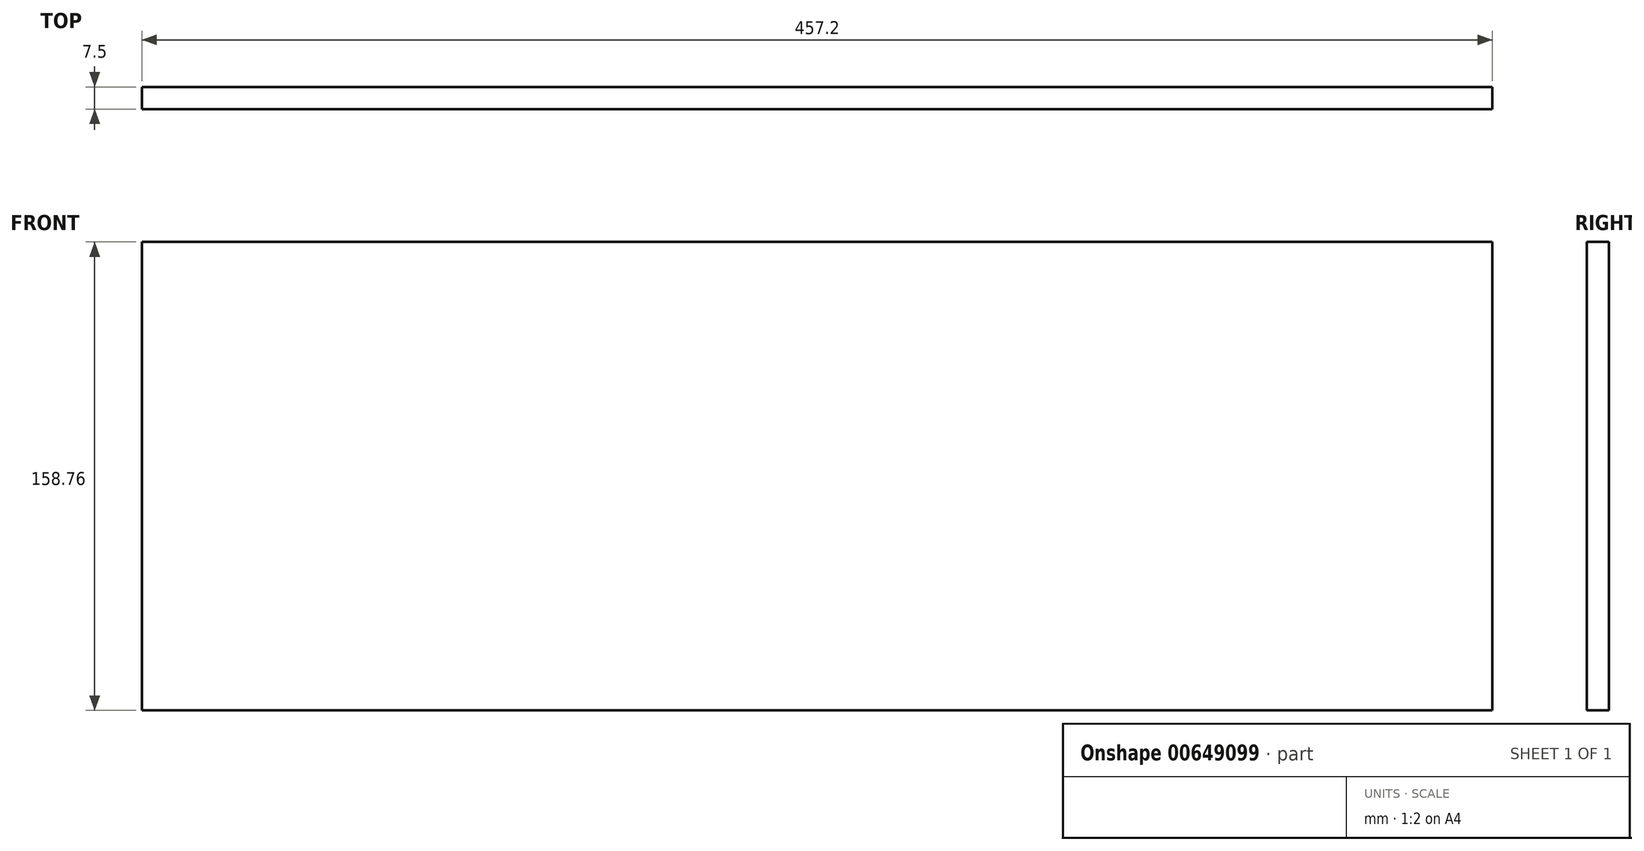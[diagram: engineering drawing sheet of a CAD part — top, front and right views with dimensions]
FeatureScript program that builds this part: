
annotation { "Feature Type Name" : "Feature", "Feature Type Description" : "" }
export const myFeature = defineFeature(function(context is Context, id is Id, definition is map)
    precondition{}
    {
        {
            var Q0;
            Q0=qCreatedBy(makeId("Front.planeOp"),FACE);
            var sketch = newSketch(context, id + "F0", { "sketchPlane" : qUnion([Q0])});
            skLineSegment(sketch, "E0.bottom", {"start": v(-228.6, 79.37) * mm, "end": v(228.6, 79.37) * mm});
            skLineSegment(sketch, "E0.top", {"start": v(-228.6, -79.37) * mm, "end": v(228.6, -79.37) * mm});
            skLineSegment(sketch, "E0.left", {"start": v(-228.6, 79.37) * mm, "end": v(-228.6, -79.37) * mm});
            skLineSegment(sketch, "E0.right", {"start": v(228.6, 79.37) * mm, "end": v(228.6, -79.37) * mm});
            skPoint(sketch, "E0.middle", {"position": v(0, 0) * mm});
            skSolve(sketch);
        }
        {
            var Q0;
            Q0=makeQuery(id+"F0.imprint","IMPRINT",FACE,{"disambiguationData":[TD([[makeQuery(id+"F0.imprint","IMPRINT",EDGE,{"derivedFrom":sQuery(id+"F0.wireOp",EDGE,"E0.bottom")}),-1.0]])]});
            extrude(context, id + "F1", {"entities" : qUnion([Q0]), "depth" : 7.5 * mm, "offsetDistance" : 25.4 * mm});
        }
    });
